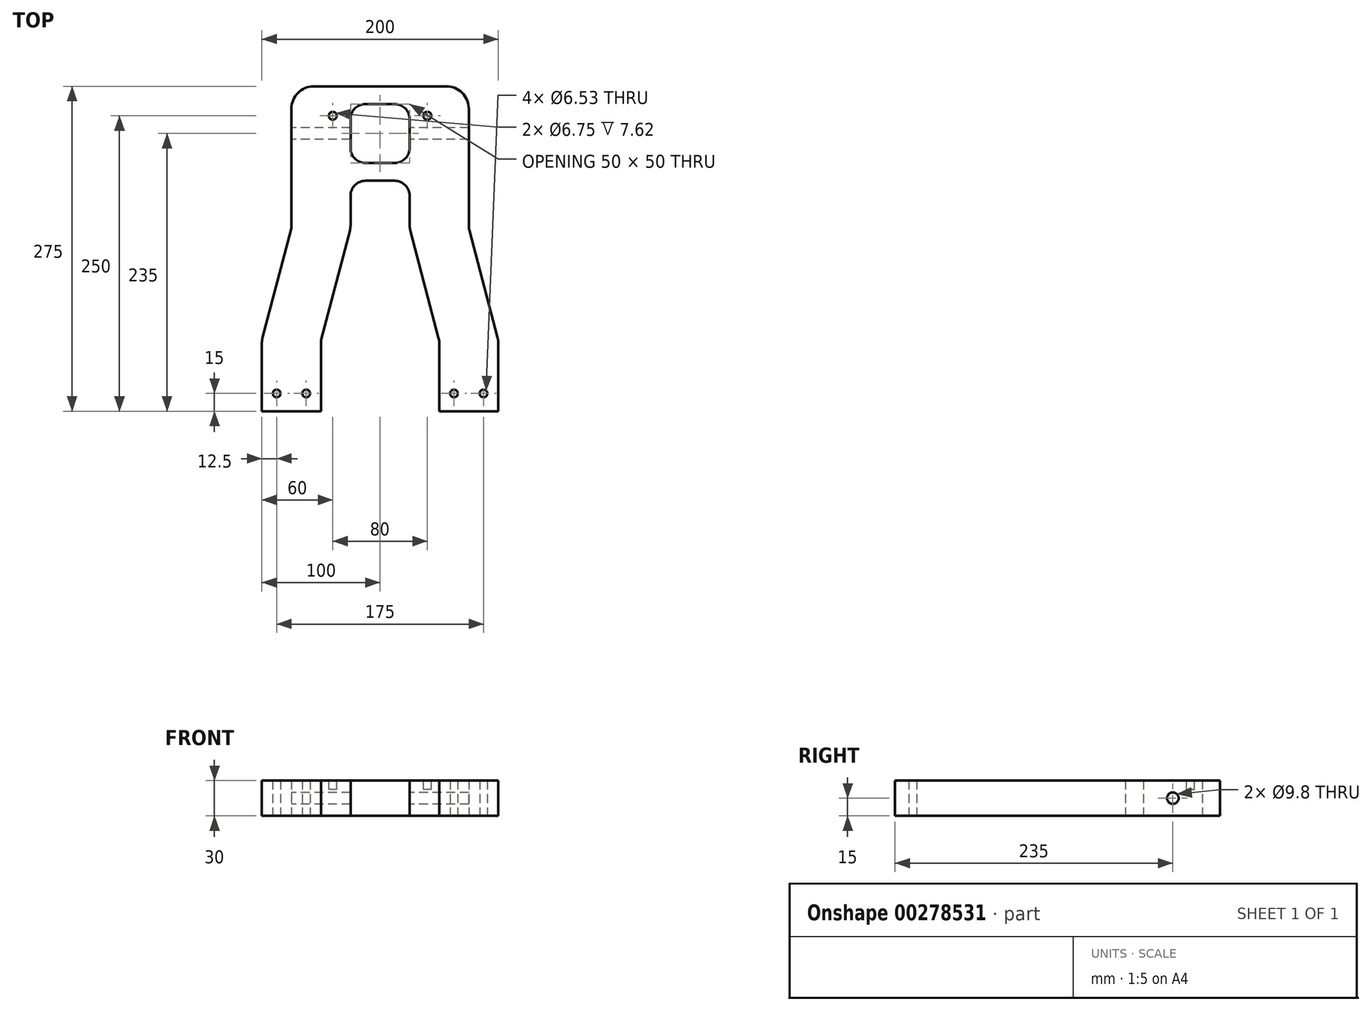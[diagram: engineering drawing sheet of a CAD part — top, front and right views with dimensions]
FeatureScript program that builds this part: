
annotation { "Feature Type Name" : "Feature", "Feature Type Description" : "" }
export const myFeature = defineFeature(function(context is Context, id is Id, definition is map)
    precondition{}
    {
        {
            var Q0;
            Q0=qCreatedBy(makeId("Top.planeOp"),FACE);
            var sketch = newSketch(context, id + "F0", { "sketchPlane" : qUnion([Q0])});
            skLineSegment(sketch, "E0.bottom", {"start": v(50, 137.5) * mm, "end": v(-50, 137.5) * mm, "construction": true});
            skLineSegment(sketch, "E0.top", {"start": v(50, -137.5) * mm, "end": v(-50, -137.5) * mm, "construction": true});
            skLineSegment(sketch, "E0.left", {"start": v(50, 137.5) * mm, "end": v(50, -137.5) * mm, "construction": true});
            skLineSegment(sketch, "E0.right", {"start": v(-50, 137.5) * mm, "end": v(-50, -137.5) * mm, "construction": true});
            skPoint(sketch, "E0.middle", {"position": v(0, 0) * mm});
            skLineSegment(sketch, "E1", {"start": v(-50, -137.5) * mm, "end": v(-100, -137.5) * mm});
            skLineSegment(sketch, "E2", {"start": v(-100, -137.5) * mm, "end": v(-100, -77.5) * mm});
            skLineSegment(sketch, "E3", {"start": v(-100, -77.5) * mm, "end": v(-75, 17.5) * mm});
            skLineSegment(sketch, "E4", {"start": v(-75, 17.5) * mm, "end": v(-75, 137.5) * mm});
            skLineSegment(sketch, "E5", {"start": v(-75, 137.5) * mm, "end": v(75, 137.5) * mm});
            skLineSegment(sketch, "E6", {"start": v(75, 137.5) * mm, "end": v(75, 17.5) * mm});
            skLineSegment(sketch, "E7", {"start": v(75, 17.5) * mm, "end": v(100, -77.5) * mm});
            skLineSegment(sketch, "E8", {"start": v(100, -77.5) * mm, "end": v(100, -137.5) * mm});
            skLineSegment(sketch, "E9", {"start": v(100, -137.5) * mm, "end": v(50, -137.5) * mm});
            skLineSegment(sketch, "E10", {"start": v(-50, -137.5) * mm, "end": v(-50, -77.5) * mm});
            skLineSegment(sketch, "E11", {"start": v(-50, -77.5) * mm, "end": v(-25, 17.5) * mm});
            skLineSegment(sketch, "E12", {"start": v(-25, 17.5) * mm, "end": v(-25, 57.5) * mm});
            skLineSegment(sketch, "E13", {"start": v(-25, 57.5) * mm, "end": v(25, 57.5) * mm});
            skLineSegment(sketch, "E14", {"start": v(25, 57.5) * mm, "end": v(25, 17.5) * mm});
            skLineSegment(sketch, "E15", {"start": v(25, 17.5) * mm, "end": v(50, -77.5) * mm});
            skLineSegment(sketch, "E16", {"start": v(50, -77.5) * mm, "end": v(50, -137.5) * mm});
            skLineSegment(sketch, "E17", {"start": v(-100, -122.5) * mm, "end": v(-50, -122.5) * mm, "construction": true});
            skLineSegment(sketch, "E18", {"start": v(100, -122.5) * mm, "end": v(50, -122.5) * mm, "construction": true});
            skCircle(sketch, "E19", {"center": v(-87.5, -122.5) * mm, "radius": 3.26 * mm});
            skCircle(sketch, "E20", {"center": v(-62.5, -122.5) * mm, "radius": 3.26 * mm});
            skCircle(sketch, "E21", {"center": v(62.5, -122.5) * mm, "radius": 3.26 * mm});
            skCircle(sketch, "E22", {"center": v(87.5, -122.5) * mm, "radius": 3.26 * mm});
            skLineSegment(sketch, "E23.bottom", {"start": v(40, 112.5) * mm, "end": v(-40, 112.5) * mm, "construction": true});
            skLineSegment(sketch, "E23.top", {"start": v(40, -112.5) * mm, "end": v(-40, -112.5) * mm, "construction": true});
            skLineSegment(sketch, "E23.left", {"start": v(40, 112.5) * mm, "end": v(40, -112.5) * mm, "construction": true});
            skLineSegment(sketch, "E23.right", {"start": v(-40, 112.5) * mm, "end": v(-40, -112.5) * mm, "construction": true});
            skCircle(sketch, "E24", {"center": v(-40, 112.5) * mm, "radius": 3.37 * mm});
            skCircle(sketch, "E25", {"center": v(40, 112.5) * mm, "radius": 3.37 * mm});
            skLineSegment(sketch, "E26", {"start": v(0, 57.5) * mm, "end": v(0, 137.5) * mm, "construction": true});
            skLineSegment(sketch, "E27.bottom", {"start": v(25, 122.5) * mm, "end": v(-25, 122.5) * mm});
            skLineSegment(sketch, "E27.top", {"start": v(25, 72.5) * mm, "end": v(-25, 72.5) * mm});
            skLineSegment(sketch, "E27.left", {"start": v(25, 122.5) * mm, "end": v(25, 72.5) * mm});
            skLineSegment(sketch, "E27.right", {"start": v(-25, 122.5) * mm, "end": v(-25, 72.5) * mm});
            skPoint(sketch, "E27.middle", {"position": v(0, 97.5) * mm});
            skSolve(sketch);
        }
        {
            var Q0;
            Q0 = qSketchRegion(id + "F0", true);
            var Q1;
            Q1=makeQuery(id+"F0.imprint","IMPRINT",FACE,{"disambiguationData":[TD([[makeQuery(id+"F0.imprint","IMPRINT",EDGE,{"derivedFrom":sQuery(id+"F0.wireOp",EDGE,"E24")}),1.0]])]});
            var Q2;
            Q2=makeQuery(id+"F0.imprint","IMPRINT",FACE,{"disambiguationData":[TD([[makeQuery(id+"F0.imprint","IMPRINT",EDGE,{"derivedFrom":sQuery(id+"F0.wireOp",EDGE,"E25")}),1.0]])]});
            extrude(context, id + "F1", {"entities" : qUnion([Q0, Q1, Q2]), "depth" : 30 * mm});
        }
        {
            var Q0;
            Q0=makeQuery(id+"F1.opExtrude","SWEPT_EDGE",EDGE,{"disambiguationData":[OSD([sQuery(id+"F0.wireOp",EDGE,"E27.bottom"),sQuery(id+"F0.wireOp",EDGE,"E27.right")])]});
            var Q1;
            Q1=makeQuery(id+"F1.opExtrude","SWEPT_EDGE",EDGE,{"disambiguationData":[OSD([sQuery(id+"F0.wireOp",EDGE,"E27.bottom"),sQuery(id+"F0.wireOp",EDGE,"E27.left")])]});
            var Q2;
            Q2=makeQuery(id+"F1.opExtrude","SWEPT_EDGE",EDGE,{"disambiguationData":[OSD([sQuery(id+"F0.wireOp",EDGE,"E27.top"),sQuery(id+"F0.wireOp",EDGE,"E27.left")])]});
            var Q3;
            Q3=makeQuery(id+"F1.opExtrude","SWEPT_EDGE",EDGE,{"disambiguationData":[OSD([sQuery(id+"F0.wireOp",EDGE,"E27.top"),sQuery(id+"F0.wireOp",EDGE,"E27.right")])]});
            var Q4;
            Q4=makeQuery(id+"F1.opExtrude","SWEPT_EDGE",EDGE,{"disambiguationData":[OSD([sQuery(id+"F0.wireOp",EDGE,"E12"),sQuery(id+"F0.wireOp",EDGE,"E13")])]});
            var Q5;
            Q5=makeQuery(id+"F1.opExtrude","SWEPT_EDGE",EDGE,{"disambiguationData":[OSD([sQuery(id+"F0.wireOp",EDGE,"E13"),sQuery(id+"F0.wireOp",EDGE,"E14")])]});
            var Q6;
            Q6=makeQuery(id+"F1.opExtrude","SWEPT_EDGE",EDGE,{"disambiguationData":[OSD([sQuery(id+"F0.wireOp",EDGE,"E15"),sQuery(id+"F0.wireOp",EDGE,"E16")])]});
            var Q7;
            Q7=makeQuery(id+"F1.opExtrude","SWEPT_EDGE",EDGE,{"disambiguationData":[OSD([sQuery(id+"F0.wireOp",EDGE,"E10"),sQuery(id+"F0.wireOp",EDGE,"E11")])]});
            var Q8;
            Q8=makeQuery(id+"F1.opExtrude","SWEPT_EDGE",EDGE,{"disambiguationData":[OSD([sQuery(id+"F0.wireOp",EDGE,"E3"),sQuery(id+"F0.wireOp",EDGE,"E4")])]});
            var Q9;
            Q9=makeQuery(id+"F1.opExtrude","SWEPT_EDGE",EDGE,{"disambiguationData":[OSD([sQuery(id+"F0.wireOp",EDGE,"E6"),sQuery(id+"F0.wireOp",EDGE,"E7")])]});
            fillet(context, id + "F2", {"entities" : qUnion([Q0, Q1, Q2, Q3, Q4, Q5, Q6, Q7, Q8, Q9]), "radius" : 12.7 * mm, "tangentPropagation" : true, "allowEdgeOverflow" : false});
        }
        {
            var Q0;
            Q0=makeQuery(id+"F1.opExtrude","SWEPT_EDGE",EDGE,{"disambiguationData":[OSD([sQuery(id+"F0.wireOp",EDGE,"E2"),sQuery(id+"F0.wireOp",EDGE,"E3")])]});
            var Q1;
            Q1=makeQuery(id+"F1.opExtrude","SWEPT_EDGE",EDGE,{"disambiguationData":[OSD([sQuery(id+"F0.wireOp",EDGE,"E4"),sQuery(id+"F0.wireOp",EDGE,"E5")])]});
            var Q2;
            Q2=makeQuery(id+"F1.opExtrude","SWEPT_EDGE",EDGE,{"disambiguationData":[OSD([sQuery(id+"F0.wireOp",EDGE,"E5"),sQuery(id+"F0.wireOp",EDGE,"E6")])]});
            var Q3;
            Q3=makeQuery(id+"F1.opExtrude","SWEPT_EDGE",EDGE,{"disambiguationData":[OSD([sQuery(id+"F0.wireOp",EDGE,"E7"),sQuery(id+"F0.wireOp",EDGE,"E8")])]});
            var Q4;
            Q4=makeQuery(id+"F1.opExtrude","SWEPT_EDGE",EDGE,{"disambiguationData":[OSD([sQuery(id+"F0.wireOp",EDGE,"E14"),sQuery(id+"F0.wireOp",EDGE,"E15")])]});
            var Q5;
            Q5=makeQuery(id+"F1.opExtrude","SWEPT_EDGE",EDGE,{"disambiguationData":[OSD([sQuery(id+"F0.wireOp",EDGE,"E11"),sQuery(id+"F0.wireOp",EDGE,"E12")])]});
            fillet(context, id + "F3", {"entities" : qUnion([Q0, Q1, Q2, Q3, Q4, Q5]), "radius" : 19.05 * mm, "tangentPropagation" : true, "allowEdgeOverflow" : false});
        }
        {
            var Q0;
            Q0=makeQuery(id+"F1.opExtrude","CAP_FACE",FACE,{"disambiguationData":[OSD([sQuery(id+"F0.wireOp",EDGE,"E1"),sQuery(id+"F0.wireOp",EDGE,"E2"),sQuery(id+"F0.wireOp",EDGE,"E3"),sQuery(id+"F0.wireOp",EDGE,"E4"),sQuery(id+"F0.wireOp",EDGE,"E5"),sQuery(id+"F0.wireOp",EDGE,"E6"),sQuery(id+"F0.wireOp",EDGE,"E7"),sQuery(id+"F0.wireOp",EDGE,"E8"),sQuery(id+"F0.wireOp",EDGE,"E9"),sQuery(id+"F0.wireOp",EDGE,"E10"),sQuery(id+"F0.wireOp",EDGE,"E11"),sQuery(id+"F0.wireOp",EDGE,"E12"),sQuery(id+"F0.wireOp",EDGE,"E13"),sQuery(id+"F0.wireOp",EDGE,"E14"),sQuery(id+"F0.wireOp",EDGE,"E15"),sQuery(id+"F0.wireOp",EDGE,"E16"),sQuery(id+"F0.wireOp",EDGE,"E19"),sQuery(id+"F0.wireOp",EDGE,"E20"),sQuery(id+"F0.wireOp",EDGE,"E21"),sQuery(id+"F0.wireOp",EDGE,"E22"),sQuery(id+"F0.wireOp",EDGE,"E27.bottom"),sQuery(id+"F0.wireOp",EDGE,"E27.top"),sQuery(id+"F0.wireOp",EDGE,"E27.left"),sQuery(id+"F0.wireOp",EDGE,"E27.right")])],"isStart":false});
            var sketch = newSketch(context, id + "F4", { "sketchPlane" : qUnion([Q0])});
            skLineSegment(sketch, "E28.bottom", {"start": v(40, 112.5) * mm, "end": v(-40, 112.5) * mm, "construction": true});
            skLineSegment(sketch, "E28.top", {"start": v(40, -112.5) * mm, "end": v(-40, -112.5) * mm, "construction": true});
            skLineSegment(sketch, "E28.left", {"start": v(40, 112.5) * mm, "end": v(40, -112.5) * mm, "construction": true});
            skLineSegment(sketch, "E28.right", {"start": v(-40, 112.5) * mm, "end": v(-40, -112.5) * mm, "construction": true});
            skPoint(sketch, "E28.middle", {"position": v(0, 0) * mm});
            skCircle(sketch, "E29", {"center": v(-40, 112.5) * mm, "radius": 3.37 * mm});
            skCircle(sketch, "E30", {"center": v(40, 112.5) * mm, "radius": 3.37 * mm});
            skSolve(sketch);
        }
        {
            var Q0;
            Q0=makeQuery(id+"F4.imprint","IMPRINT",FACE,{"disambiguationData":[TD([[makeQuery(id+"F4.imprint","IMPRINT",EDGE,{"derivedFrom":sQuery(id+"F4.wireOp",EDGE,"E29")}),1.0]])]});
            var Q1;
            Q1=makeQuery(id+"F4.imprint","IMPRINT",FACE,{"disambiguationData":[TD([[makeQuery(id+"F4.imprint","IMPRINT",EDGE,{"derivedFrom":sQuery(id+"F4.wireOp",EDGE,"E30")}),1.0]])]});
            var Q2;
            Q2=sQuery(id+"F4.wireOp",EDGE,"E29");
            extrude(context, id + "F5", {"entities" : qUnion([Q0, Q1]), "operationType" : NewBodyOperationType.REMOVE, "surfaceEntities" : qUnion([Q2]), "oppositeDirection" : true, "depth" : 7.62 * mm});
        }
        {
            var Q0;
            Q0=makeQuery(id+"F1.opExtrude","SWEPT_FACE",FACE,{"disambiguationData":[OSD([sQuery(id+"F0.wireOp",EDGE,"E4")])]});
            var sketch = newSketch(context, id + "F6", { "sketchPlane" : qUnion([Q0])});
            skCircle(sketch, "E31", {"center": v(-97.5, 15) * mm, "radius": 4.9 * mm});
            skLineSegment(sketch, "E32", {"start": v(-19.14, 15) * mm, "end": v(-118.45, 15) * mm, "construction": true});
            skSolve(sketch);
        }
        {
            var Q0;
            Q0 = qSketchRegion(id + "F6", true);
            extrude(context, id + "F7", {"entities" : qUnion([Q0]), "operationType" : NewBodyOperationType.REMOVE, "endBound" : BoundingType.THROUGH_ALL, "oppositeDirection" : true, "depth" : 25 * mm});
        }
    });
